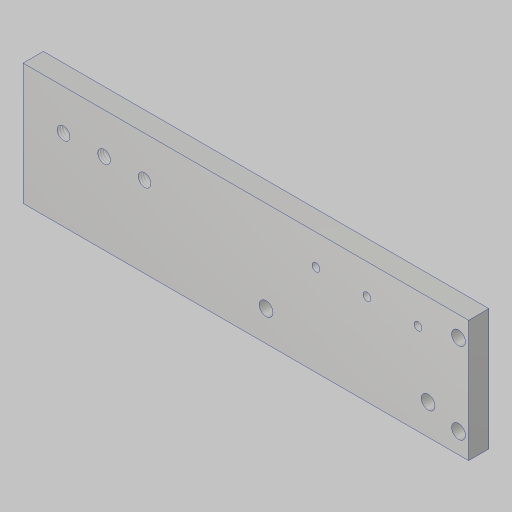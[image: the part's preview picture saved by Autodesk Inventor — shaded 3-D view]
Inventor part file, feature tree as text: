
AUTODESK INVENTOR PART (.ipt)
format: ipt  version: 2023.5 (Build 275446000, 446)  size: 147,456 bytes
history: native  units: in
note: dims shown in document units (in); Inventor stores cm internally (conversion verified against a paired STEP export)
features: sketch x4, hole x3, extrude x1
ambient origin geometry x8: Origin, YZ Plane, XZ Plane, XY Plane, X Axis, Y Axis, Z Axis, Center Point
bodies: Solid1 (feature_tree)
feature tree (8):
  extrude  "Extrusion1"  Depth=1.5in
  hole  "Hole1"  [1 undecoded]
  hole  "Hole2"  [1 undecoded]
  hole  "Hole3"  [1 undecoded]
  sketch  "Sketch1"  dims[d0=5.5in d1=1.5in]
  sketch  "Sketch2"  dims[d2=0.25in d3=0.0in d4=0.5in d5=0.5in]
  sketch  "Sketch3"  dims[d6=0.5in]
  sketch  "Sketch6"  dims[d7=0.156in d8=0.38in d9=0.385in d10=0.25in d11=0.5635in d12=1.0in d13=0.8108in d14=0.5in d15=0.5in d16=0.25in d17=0.25in d18=0.125in d19=0.17in d20=0.328in d21=0.332in d22=0.25in d23=0.5635in d24=1.0in d25=0.8108in d30=1.2598in d32=0.0968in d33=0.236in d34=0.385in d35=0.25in d36=0.5635in d37=1.0in d38=0.8108in d39=2.0in d41=1.125in d43=0.5in d44=0.625in d45=1.125in]
note: 3 required parameter values undecoded (feature->parameter linkage not recoverable at this tier; creation-order binding heuristic only, values carry confidence <= 0.55)
